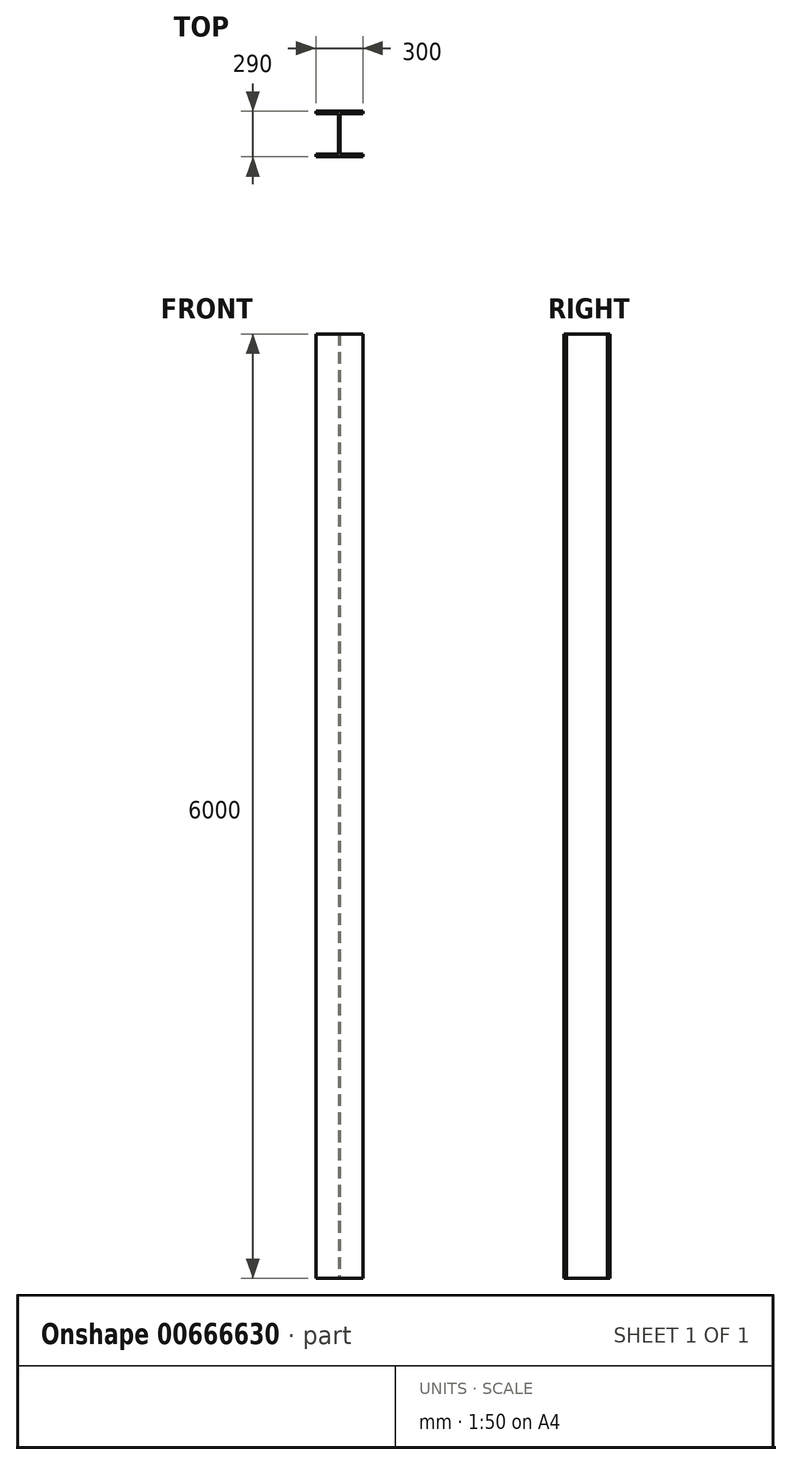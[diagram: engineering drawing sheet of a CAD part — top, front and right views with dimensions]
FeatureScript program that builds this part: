
annotation { "Feature Type Name" : "Feature", "Feature Type Description" : "" }
export const myFeature = defineFeature(function(context is Context, id is Id, definition is map)
    precondition{}
    {
        {
            var Q0;
            Q0=qCreatedBy(makeId("Top.planeOp"),FACE);
            var sketch = newSketch(context, id + "F0", { "sketchPlane" : qUnion([Q0])});
            skLineSegment(sketch, "E0", {"start": v(-23.12, -10.88) * mm, "end": v(276.88, -10.88) * mm});
            skLineSegment(sketch, "E1", {"start": v(276.88, -10.88) * mm, "end": v(276.88, 4.12) * mm});
            skLineSegment(sketch, "E2", {"start": v(276.88, 4.12) * mm, "end": v(131.88, 4.12) * mm});
            skLineSegment(sketch, "E3", {"start": v(131.88, 4.12) * mm, "end": v(131.88, 264.12) * mm});
            skLineSegment(sketch, "E4", {"start": v(131.88, 264.12) * mm, "end": v(276.88, 264.12) * mm});
            skLineSegment(sketch, "E5", {"start": v(276.88, 264.12) * mm, "end": v(276.88, 279.12) * mm});
            skLineSegment(sketch, "E6", {"start": v(276.88, 279.12) * mm, "end": v(-23.12, 279.12) * mm});
            skLineSegment(sketch, "E7", {"start": v(-23.12, 279.12) * mm, "end": v(-23.12, 264.12) * mm});
            skPoint(sketch, "E7.endSnap0", {"position": v(204.38, 264.12) * mm});
            skLineSegment(sketch, "E8", {"start": v(-23.12, 264.12) * mm, "end": v(121.88, 264.12) * mm});
            skLineSegment(sketch, "E9", {"start": v(121.88, 264.12) * mm, "end": v(121.88, 4.12) * mm});
            skLineSegment(sketch, "E10", {"start": v(121.88, 4.12) * mm, "end": v(-23.12, 4.12) * mm});
            skLineSegment(sketch, "E11", {"start": v(-23.12, 4.12) * mm, "end": v(-23.12, -10.88) * mm});
            skSolve(sketch);
        }
        {
            var Q0;
            Q0=makeQuery(id+"F0.imprint","IMPRINT",FACE,{"disambiguationData":[TD([[makeQuery(id+"F0.imprint","IMPRINT",EDGE,{"derivedFrom":sQuery(id+"F0.wireOp",EDGE,"E0")}),1.0]])]});
            extrude(context, id + "F1", {"entities" : qUnion([Q0]), "depth" : 6000 * mm, "offsetDistance" : 25 * mm});
        }
    });
